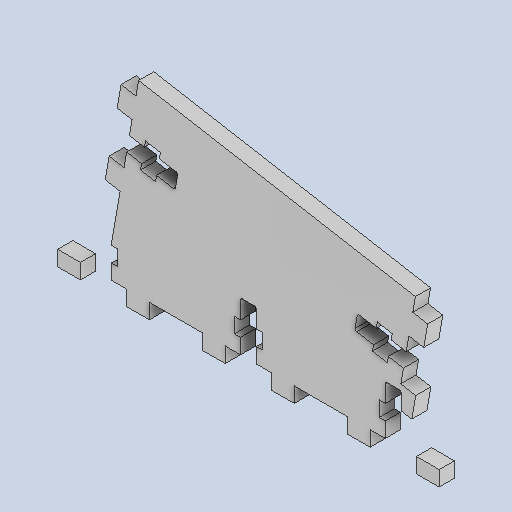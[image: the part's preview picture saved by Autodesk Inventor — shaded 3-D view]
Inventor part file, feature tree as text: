
AUTODESK INVENTOR PART (.ipt)
format: ipt  version: 2024.1 (Build 281209000, 209)  size: 456,704 bytes
history: native  units: mm
features: other x9, extrude x1, sketch x1
ambient origin geometry x8: Origin, YZ Plane, XZ Plane, XY Plane, X Axis, Y Axis, Z Axis, Center Point
bodies: Solide1 (feature_tree)
feature tree (11):
  other  "shared_parameters.ipt"
  other  "Blocs"
  extrude  "Extrusion1"  Depth=10.0mm
  other  "Anchor (screw side)"
  other  "Anchor (nut side)"
  sketch  "Esquisse2"
  other  "Anchor (nut side):1"
  other  "Anchor (nut side):2"
  other  "Anchor (nut side):3"
  other  "Anchor (nut side):4"
  other  "Anchor (nut side):5"
